# Revit family: VOY1_63_UN_Inlay LED_ETK
name_source: partatom
category: Lighting Fixtures
revit_build: Autodesk Revit 2017 (Build: 20190508_0315(x64)
units: mm (PartAtom-declared; Revit-internal decimal feet)

## family parameters
Always vertical = Yes
Cut with Voids When Loaded = No
Light Source = No
OmniClass Number = 23.80.70.11.14.11
OmniClass Title = Downlights
Part Type = Normal
Room Calculation Point = Yes
Round Connector Dimension = Use Diameter
Shared = No
Work Plane-Based = No

## types (4) — shared parameters
Apparent Load = 34 VA
Assembly Code = 63.0
Bundle = 85°
Description = Recessed/inlay LED
IfcExportAs = IfcLightFixtureType
IfcExportType = USERDEFINED
Lamp = LED
Luminaire_Body_Material = PPS Plastic
Manufacturer = ETK licht B.V.
Model = VOY.1
URL = https://www.etk.nl
Voltage = 230 V
Wattage Comments = 34W

## per-type parameters (varying)
| type | Light Source |
| VOY.1110.10 - 34W / 3700lm / 3000K | VOY.1 - Lightsource : VOY.1110.10 - 34W / 3700lm / 3000K |
| VOY.1113.10 - 34W / 3700lm / 3000K | VOY.1 - Lightsource : VOY.1113.10 - 34W / 3700lm / 3000K |
| VOY.1210.10 - 34W / 3800lm / 4000K | VOY.1 - Lightsource : VOY.1210.10 - 34W / 3800lm / 4000K |
| VOY.1213.10 - 34W / 3800lm / 4000K | VOY.1 - Lightsource : VOY.1213.10 - 34W / 3800lm / 4000K |

## geometry (parser evidence)
native form markers: Sweep x6
no freeform markers — native parametric forms only
